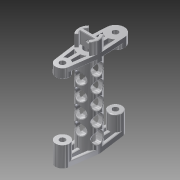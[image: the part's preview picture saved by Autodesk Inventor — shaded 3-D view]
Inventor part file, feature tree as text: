
AUTODESK INVENTOR PART (.ipt)
format: ipt  version: 2014 (Build 180170000, 170)  size: 1,133,056 bytes
history: native  units: mm
features: extrude x10, sketch x6, fillet x3, mirror x2, plane x1, pattern_linear x1
ambient origin geometry x8: Origin, YZ Plane, XZ Plane, XY Plane, X Axis, Y Axis, Z Axis, Center Point
bodies: Solid1 (feature_tree)
feature tree (23):
  extrude  "Extrusion1"  Depth=4.0mm
  extrude  "Extrusion2"  Depth=4.0mm
  extrude  "Extrusion3"  Depth=4.0mm
  plane  "Work Plane1"
  extrude  "Extrusion4"  Depth=2.0mm
  extrude  "Extrusion5"  Depth=2.0mm
  extrude  "Extrusion9"  Depth=4.0mm
  extrude  "Extrusion10"  Depth=4.0mm
  fillet  "Fillet1"  Radius=4.0mm
  fillet  "Fillet2"  Radius=2.0mm
  extrude  "Extrusion11"  Depth=2.0mm
  fillet  "Fillet3"  Radius=6.0mm
  extrude  "Extrusion12"  Depth=4.0mm TaperAngle=0.0deg
  sketch  "Sketch7"  dims[d12=2.0mm d13=5.0mm]
  extrude  "Extrusion14"  TaperAngle=0.0deg  [1 undecoded]
  mirror  "Mirror2"
  mirror  "Mirror3"
  pattern_linear  "Rectangular Pattern3"  Spacing1=108.0mm  [1 undecoded]
  sketch  "Sketch3"  dims[d2=4.0mm d3=7.0mm]
  sketch  "Sketch4"  dims[d5=13.0mm d7=4.0mm]
  sketch  "Sketch5"  dims[d8=4.0mm d9=4.0mm]
  sketch  "Sketch6"  dims[d10=4.0mm d11=2.0mm]
  sketch  "Sketch10"  dims[d14=6.5mm d16=7.0mm d17=5.0mm d18=4.0mm d19=2.0mm d20=2.0mm d22=6.0mm d23=0.0mm d24=25.0mm d25=0.0mm d27=0.0mm d28=108.0mm d31=10.0mm d34=5.0mm d35=5.0mm d36=5.0mm d37=5.0mm d38=10.0mm d39=45.0deg d40=4.0mm d41=4.0mm d42=4.0mm d43=2.0mm d44=4.0mm d45=6.0mm d46=0.0mm d47=12.0mm d48=0.0mm d49=10.0mm d50=10.0mm d51=30.0mm d52=30.0mm d53=10.0mm d54=46.0mm d62=6.0mm d63=0.0mm d64=14.0mm d65=30.0mm d66=0.0mm d70=14.0mm d71=14.0mm d72=14.0mm d73=14.0mm d74=4.333333mm d75=4.333333mm d76=4.333333mm d77=4.333333mm d78=4.333333mm d79=4.333333mm d80=13.0mm d81=13.0mm d82=13.0mm d83=13.0mm d84=13.0mm d85=13.0mm d86=14.0mm d87=4.333333mm d88=14.0mm d89=14.0mm d90=14.0mm d91=4.333333mm d92=4.333333mm d93=26.5mm d94=26.5mm d95=30.0mm d96=0.0mm d97=1.0mm d98=1.0mm d99=4.0mm d100=2.0mm d101=2.0mm d102=45.0deg d103=45.0deg d104=15.0mm d105=0.0mm d106=1.0mm d107=20.0mm d108=26.0mm d109=7.5mm d110=8.774964mm d111=8.774964mm d112=4.0mm d113=10.0mm d114=0.0mm d115=66.0mm d121=12.763383mm d122=12.763383mm d139=5.0mm d140=0.0mm d141=10.0mm d142=10.0mm d143=10.0mm d144=0.672936mm d145=0.672936mm d146=0.672936mm d147=0.672936mm d148=2.0mm d149=1.5mm d150=1.5mm d151=4.0mm d152=0.0mm d153=20.0mm d155=103.0mm d156=5.0mm d157=0.0mm d158=10.922mm d159=20.0mm d160=20.0mm]
note: 2 required parameter values undecoded (feature->parameter linkage not recoverable at this tier; creation-order binding heuristic only, values carry confidence <= 0.55)
